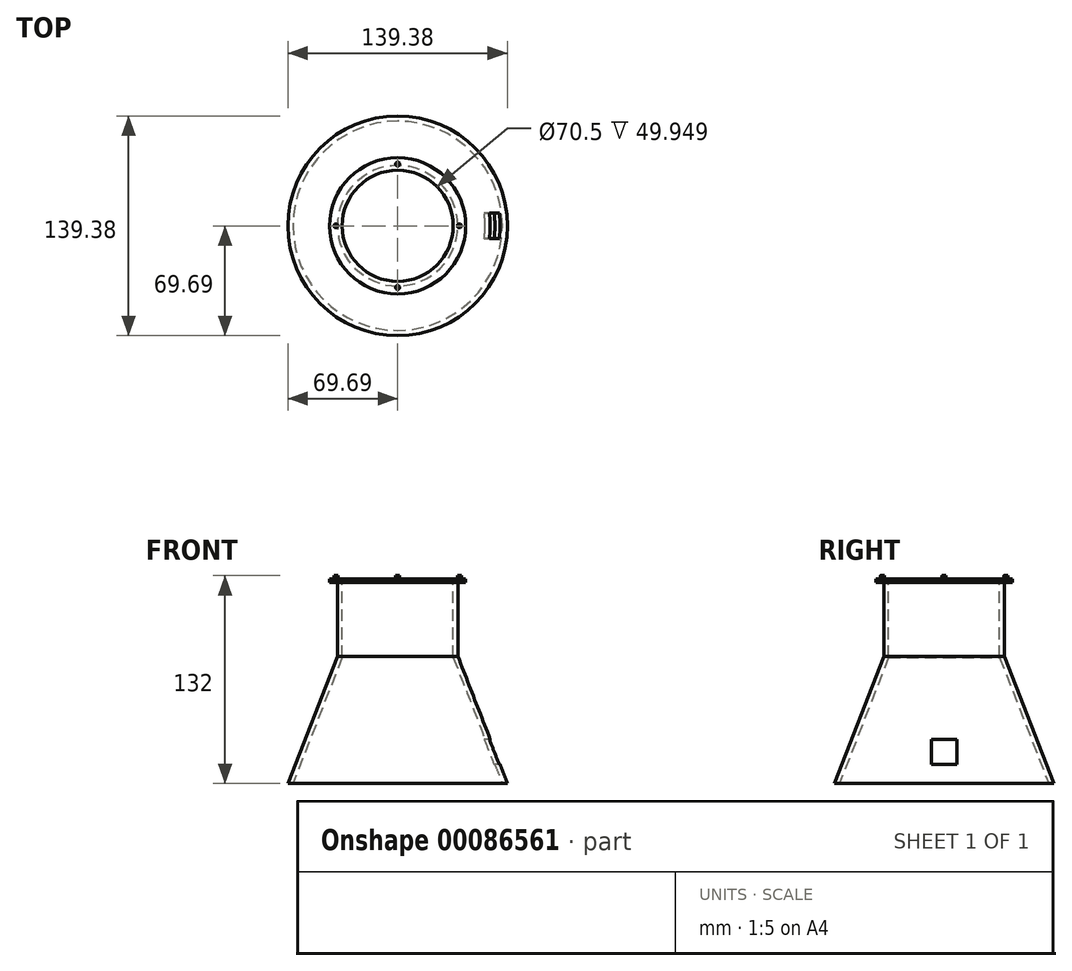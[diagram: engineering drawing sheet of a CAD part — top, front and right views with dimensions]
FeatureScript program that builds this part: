
annotation { "Feature Type Name" : "Feature", "Feature Type Description" : "" }
export const myFeature = defineFeature(function(context is Context, id is Id, definition is map)
    precondition{}
    {
        {
            var Q0;
            Q0=qCreatedBy(makeId("Front.planeOp"),FACE);
            var sketch = newSketch(context, id + "F0", { "sketchPlane" : qUnion([Q0])});
            skLineSegment(sketch, "E0.bottom", {"start": v(0, 0) * mm, "end": v(35.25, 0) * mm});
            skLineSegment(sketch, "E0.top", {"start": v(0, -80) * mm, "end": v(35.25, -80) * mm});
            skLineSegment(sketch, "E0.left", {"start": v(0, 0) * mm, "end": v(0, -80) * mm});
            skLineSegment(sketch, "E0.right", {"start": v(35.25, 0) * mm, "end": v(35.25, -80) * mm});
            skLineSegment(sketch, "E1", {"start": v(0, -80) * mm, "end": v(0, -130) * mm});
            skLineSegment(sketch, "E2", {"start": v(0, -130) * mm, "end": v(66.44, -130) * mm});
            skLineSegment(sketch, "E3", {"start": v(66.44, -130) * mm, "end": v(35.25, -49.95) * mm});
            skLineSegment(sketch, "E4", {"start": v(35.25, 0) * mm, "end": v(43.25, 0) * mm});
            skLineSegment(sketch, "E5", {"start": v(43.25, 0) * mm, "end": v(43.25, -2.4) * mm});
            skLineSegment(sketch, "E6", {"start": v(43.25, -2.4) * mm, "end": v(38.25, -2.4) * mm});
            skLineSegment(sketch, "E7", {"start": v(38.25, -2.4) * mm, "end": v(38.25, -49.3) * mm});
            skLineSegment(sketch, "E8", {"start": v(38.25, -49.3) * mm, "end": v(69.7, -130) * mm});
            skLineSegment(sketch, "E9", {"start": v(69.7, -130) * mm, "end": v(66.44, -130) * mm});
            skPoint(sketch, "E10", {"position": v(35.25, -40) * mm});
            skSolve(sketch);
        }
        {
            var Q0;
            {var subQ1=sQuery(id+"F0.wireOp",EDGE,"E3");Q0=makeQuery(id+"F0.imprint","IMPRINT",FACE,{"disambiguationData":[TD([[makeQuery(id+"F0.imprint","IMPRINT",EDGE,{"derivedFrom":subQ1}),-1.0]])]});}
            var Q1;
            Q1=sQuery(id+"F0.wireOp",EDGE,"E0.left");
            revolve(context, id + "F1", {"entities" : qUnion([Q0]), "axis" : qUnion([Q1]), "revolveType" : RevolveType.FULL});
        }
        {
            var Q0;
            Q0=qCreatedBy(makeId("Right.planeOp"),FACE);
            var sketch = newSketch(context, id + "F2", { "sketchPlane" : qUnion([Q0])});
            skLineSegment(sketch, "E11.0", {"start": v(-69.7, -130) * mm, "end": v(69.7, -130) * mm});
            skLineSegment(sketch, "E12.0", {"start": v(0, -80) * mm, "end": v(0, -130) * mm});
            skLineSegment(sketch, "E13.bottom", {"start": v(-8, -102) * mm, "end": v(8, -102) * mm});
            skLineSegment(sketch, "E13.top", {"start": v(-8, -118) * mm, "end": v(8, -118) * mm});
            skLineSegment(sketch, "E13.left", {"start": v(-8, -102) * mm, "end": v(-8, -118) * mm});
            skLineSegment(sketch, "E13.right", {"start": v(8, -102) * mm, "end": v(8, -118) * mm});
            skLineSegment(sketch, "E14", {"start": v(0, -118) * mm, "end": v(0, -80) * mm});
            skLineSegment(sketch, "E15", {"start": v(0, -102) * mm, "end": v(0, -80) * mm});
            skSolve(sketch);
        }
        {
            var Q0;
            {var subQ0=sQuery(id+"F2.wireOp",EDGE,"E13.left");Q0=makeQuery(id+"F2.imprint","IMPRINT",FACE,{"disambiguationData":[TD([[makeQuery(id+"F2.imprint","IMPRINT",EDGE,{"derivedFrom":subQ0}),1.0]])]});}
            var Q1;
            {var subQ0=sQuery(id+"F2.wireOp",EDGE,"E13.right");Q1=makeQuery(id+"F2.imprint","IMPRINT",FACE,{"disambiguationData":[TD([[makeQuery(id+"F2.imprint","IMPRINT",EDGE,{"derivedFrom":subQ0}),-1.0]])]});}
            extrude(context, id + "F3", {"entities" : qUnion([Q0, Q1]), "operationType" : NewBodyOperationType.REMOVE, "depth" : 77.17 * mm});
        }
        {
            var Q0;
            Q0=makeQuery(id+"F1.opRevolve","SWEPT_FACE",FACE,{"disambiguationData":[OSD([sQuery(id+"F0.wireOp",EDGE,"E4")])]});
            var sketch = newSketch(context, id + "F4", { "sketchPlane" : qUnion([Q0])});
            skCircle(sketch, "E16", {"center": v(39.2, 0) * mm, "radius": 1.25 * mm});
            skCircle(sketch, "E17.1.0", {"center": v(0, 39.2) * mm, "radius": 1.25 * mm});
            skCircle(sketch, "E17.2.0", {"center": v(-39.2, 0) * mm, "radius": 1.25 * mm});
            skCircle(sketch, "E17.3.0", {"center": v(0, -39.2) * mm, "radius": 1.25 * mm});
            skPoint(sketch, "E17.center", {"position": v(0, 0) * mm});
            skSolve(sketch);
        }
        {
            var Q0;
            Q0=makeQuery(id+"F4.imprint","IMPRINT",FACE,{"disambiguationData":[TD([[makeQuery(id+"F4.imprint","IMPRINT",EDGE,{"derivedFrom":sQuery(id+"F4.wireOp",EDGE,"E17.1.0")}),1.0]])]});
            var Q1;
            Q1=makeQuery(id+"F4.imprint","IMPRINT",FACE,{"disambiguationData":[TD([[makeQuery(id+"F4.imprint","IMPRINT",EDGE,{"derivedFrom":sQuery(id+"F4.wireOp",EDGE,"E17.2.0")}),1.0]])]});
            var Q2;
            Q2=makeQuery(id+"F4.imprint","IMPRINT",FACE,{"disambiguationData":[TD([[makeQuery(id+"F4.imprint","IMPRINT",EDGE,{"derivedFrom":sQuery(id+"F4.wireOp",EDGE,"E17.3.0")}),1.0]])]});
            var Q3;
            Q3=makeQuery(id+"F4.imprint","IMPRINT",FACE,{"disambiguationData":[TD([[makeQuery(id+"F4.imprint","IMPRINT",EDGE,{"derivedFrom":sQuery(id+"F4.wireOp",EDGE,"E16")}),1.0]])]});
            extrude(context, id + "F5", {"entities" : qUnion([Q0, Q1, Q2, Q3]), "operationType" : NewBodyOperationType.ADD, "depth" : 2 * mm});
        }
    });
